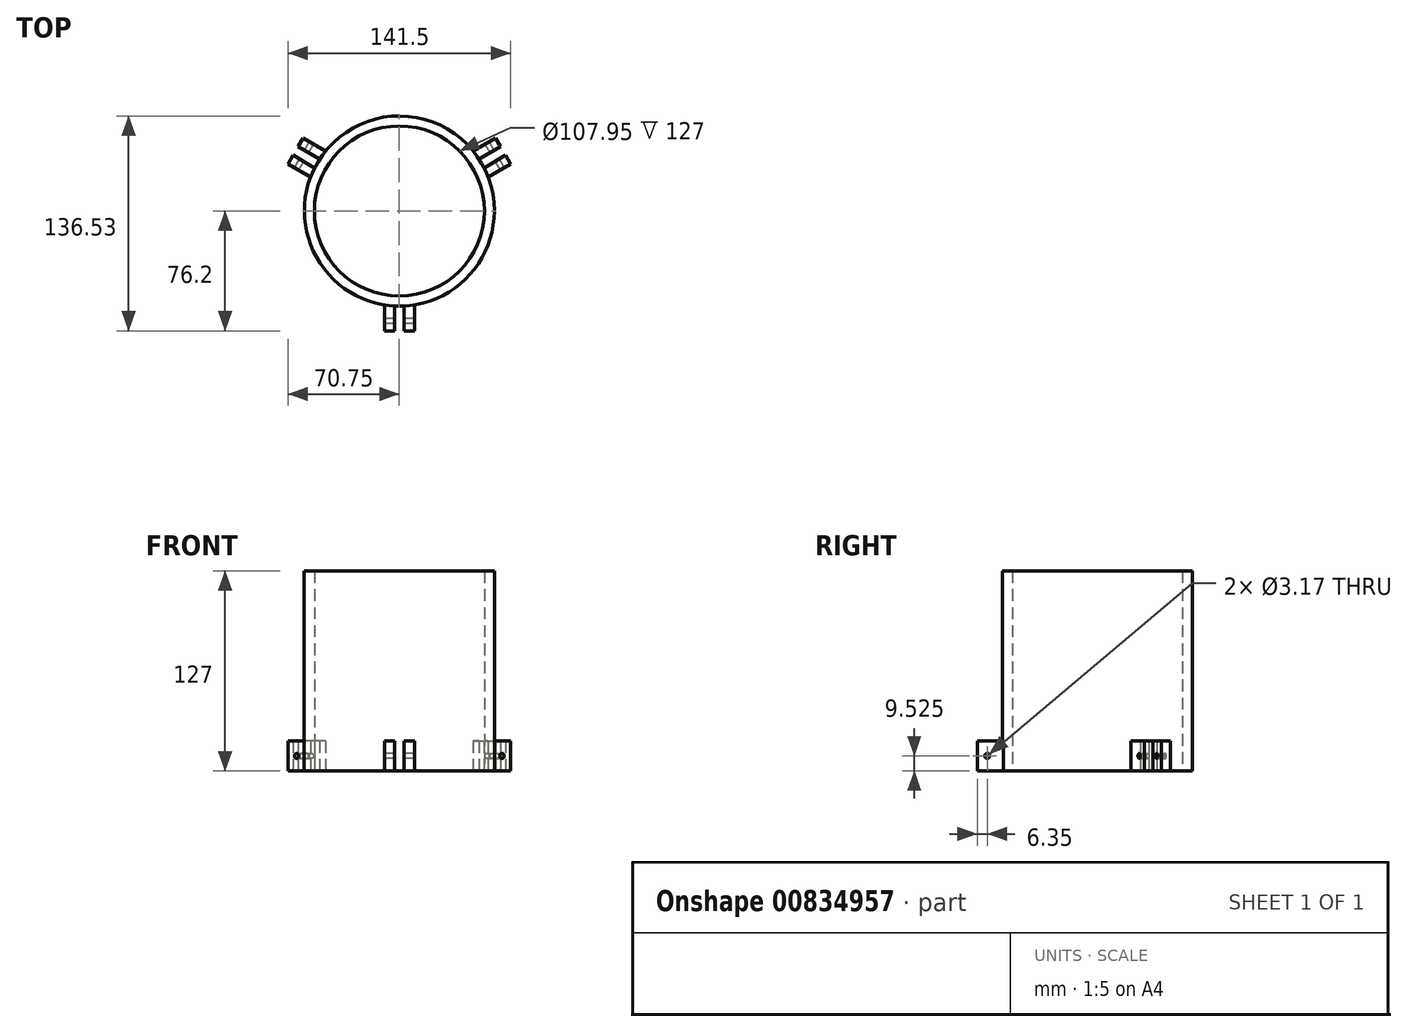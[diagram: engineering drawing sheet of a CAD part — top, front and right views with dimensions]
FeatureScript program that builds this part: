
annotation { "Feature Type Name" : "Feature", "Feature Type Description" : "" }
export const myFeature = defineFeature(function(context is Context, id is Id, definition is map)
    precondition{}
    {
        {
            var Q0;
            Q0=qCreatedBy(makeId("Top.planeOp"),FACE);
            var sketch = newSketch(context, id + "F0", { "sketchPlane" : qUnion([Q0])});
            skCircle(sketch, "E0", {"center": v(0, 0) * mm, "radius": 53.98 * mm});
            skSolve(sketch);
        }
        {
            var Q0;
            Q0=qCreatedBy(makeId("Top.planeOp"),FACE);
            var sketch = newSketch(context, id + "F1", { "sketchPlane" : qUnion([Q0])});
            skCircle(sketch, "E1", {"center": v(0, 0) * mm, "radius": 60.33 * mm});
            skSolve(sketch);
        }
        {
            var Q0;
            Q0=makeQuery(id+"F1.imprint","IMPRINT",FACE,{"disambiguationData":[TD([[makeQuery(id+"F1.imprint","IMPRINT",EDGE,{"derivedFrom":sQuery(id+"F1.wireOp",EDGE,"E1")}),1.0]])]});
            extrude(context, id + "F2", {"entities" : qUnion([Q0]), "depth" : 127 * mm, "offsetDistance" : 25.4 * mm});
        }
        {
            var Q0;
            Q0=makeQuery(id+"F0.imprint","IMPRINT",FACE,{"disambiguationData":[TD([[makeQuery(id+"F0.imprint","IMPRINT",EDGE,{"derivedFrom":sQuery(id+"F0.wireOp",EDGE,"E0")}),1.0]])]});
            extrude(context, id + "F3", {"entities" : qUnion([Q0]), "operationType" : NewBodyOperationType.REMOVE, "depth" : 184.9 * mm, "offsetDistance" : 25.4 * mm});
        }
        {
            var Q0;
            Q0=qCreatedBy(makeId("Top.planeOp"),FACE);
            var sketch = newSketch(context, id + "F4", { "sketchPlane" : qUnion([Q0])});
            skLineSegment(sketch, "E2", {"start": v(0, 0) * mm, "end": v(0, 76.2) * mm});
            skLineSegment(sketch, "E3", {"start": v(0, 0) * mm, "end": v(-66, 38.1) * mm});
            skLineSegment(sketch, "E4", {"start": v(0, 0) * mm, "end": v(66, 38.1) * mm});
            skLineSegment(sketch, "E5", {"start": v(0, 0) * mm, "end": v(0, -76.2) * mm});
            skPoint(sketch, "E6", {"position": v(-33, 19.05) * mm});
            skPoint(sketch, "E7", {"position": v(33, 19.05) * mm});
            skPoint(sketch, "E8", {"position": v(0, -38.1) * mm});
            skLineSegment(sketch, "E9.0", {"start": v(4.76, 8.25) * mm, "end": v(-61.23, 46.35) * mm});
            skLineSegment(sketch, "E10.0", {"start": v(-4.76, -8.25) * mm, "end": v(-70.75, 29.85) * mm});
            skLineSegment(sketch, "E11.0", {"start": v(4.76, -8.25) * mm, "end": v(70.75, 29.85) * mm});
            skLineSegment(sketch, "E12.0", {"start": v(-4.76, 8.25) * mm, "end": v(61.23, 46.35) * mm});
            skLineSegment(sketch, "E13.0", {"start": v(1.59, -2.75) * mm, "end": v(67.58, 35.35) * mm});
            skLineSegment(sketch, "E14.0", {"start": v(-1.59, 2.75) * mm, "end": v(64.4, 40.85) * mm});
            skLineSegment(sketch, "E15.0", {"start": v(1.59, 2.75) * mm, "end": v(-64.4, 40.85) * mm});
            skLineSegment(sketch, "E16.0", {"start": v(-1.59, -2.75) * mm, "end": v(-67.58, 35.35) * mm});
            skLineSegment(sketch, "E17.0", {"start": v(-9.53, 0) * mm, "end": v(-9.52, -76.2) * mm});
            skLineSegment(sketch, "E18.0", {"start": v(9.52, 0) * mm, "end": v(9.53, -76.2) * mm});
            skLineSegment(sketch, "E19.0", {"start": v(-3.18, 0) * mm, "end": v(-3.17, -76.2) * mm});
            skLineSegment(sketch, "E20.0", {"start": v(3.17, 0) * mm, "end": v(3.18, -76.2) * mm});
            skLineSegment(sketch, "E21", {"start": v(-70.75, 29.85) * mm, "end": v(-67.58, 35.35) * mm});
            skLineSegment(sketch, "E22", {"start": v(-64.4, 40.85) * mm, "end": v(-61.23, 46.35) * mm});
            skLineSegment(sketch, "E23", {"start": v(61.23, 46.35) * mm, "end": v(64.4, 40.85) * mm});
            skLineSegment(sketch, "E24", {"start": v(67.58, 35.35) * mm, "end": v(70.75, 29.85) * mm});
            skLineSegment(sketch, "E25", {"start": v(-9.52, -76.2) * mm, "end": v(-3.17, -76.2) * mm});
            skLineSegment(sketch, "E26", {"start": v(3.18, -76.2) * mm, "end": v(9.53, -76.2) * mm});
            skCircle(sketch, "E27", {"center": v(0, 0) * mm, "radius": 60.28 * mm});
            skSolve(sketch);
        }
        {
            var Q0;
            {var subQ0=sQuery(id+"F4.wireOp",EDGE,"E21");Q0=makeQuery(id+"F4.imprint","IMPRINT",FACE,{"disambiguationData":[TD([[makeQuery(id+"F4.imprint","IMPRINT",EDGE,{"derivedFrom":subQ0}),-1.0]])]});}
            var Q1;
            {var subQ0=sQuery(id+"F4.wireOp",EDGE,"E22");Q1=makeQuery(id+"F4.imprint","IMPRINT",FACE,{"disambiguationData":[TD([[makeQuery(id+"F4.imprint","IMPRINT",EDGE,{"derivedFrom":subQ0}),-1.0]])]});}
            var Q2;
            {var subQ0=sQuery(id+"F4.wireOp",EDGE,"E24");Q2=makeQuery(id+"F4.imprint","IMPRINT",FACE,{"disambiguationData":[TD([[makeQuery(id+"F4.imprint","IMPRINT",EDGE,{"derivedFrom":subQ0}),-1.0]])]});}
            var Q3;
            {var subQ0=sQuery(id+"F4.wireOp",EDGE,"E23");Q3=makeQuery(id+"F4.imprint","IMPRINT",FACE,{"disambiguationData":[TD([[makeQuery(id+"F4.imprint","IMPRINT",EDGE,{"derivedFrom":subQ0}),-1.0]])]});}
            var Q4;
            {var subQ0=sQuery(id+"F4.wireOp",EDGE,"E25");Q4=makeQuery(id+"F4.imprint","IMPRINT",FACE,{"disambiguationData":[TD([[makeQuery(id+"F4.imprint","IMPRINT",EDGE,{"derivedFrom":subQ0}),1.0]])]});}
            var Q5;
            {var subQ0=sQuery(id+"F4.wireOp",EDGE,"E26");Q5=makeQuery(id+"F4.imprint","IMPRINT",FACE,{"disambiguationData":[TD([[makeQuery(id+"F4.imprint","IMPRINT",EDGE,{"derivedFrom":subQ0}),1.0]])]});}
            extrude(context, id + "F5", {"entities" : qUnion([Q0, Q1, Q2, Q3, Q4, Q5]), "operationType" : NewBodyOperationType.ADD, "depth" : 19.05 * mm, "offsetDistance" : 25.4 * mm});
        }
        {
            var Q0;
            Q0=makeQuery(id+"F5.opExtrude","SWEPT_FACE",FACE,{"disambiguationData":[OSD([sQuery(id+"F4.wireOp",EDGE,"E9.0")])]});
            var sketch = newSketch(context, id + "F6", { "sketchPlane" : qUnion([Q0])});
            skCircle(sketch, "E28", {"center": v(69.85, 9.53) * mm, "radius": 1.59 * mm});
            skSolve(sketch);
        }
        {
            var Q0;
            Q0=makeQuery(id+"F6.imprint","IMPRINT",FACE,{"disambiguationData":[TD([[makeQuery(id+"F6.imprint","IMPRINT",EDGE,{"derivedFrom":sQuery(id+"F6.wireOp",EDGE,"E28")}),1.0]])]});
            extrude(context, id + "F7", {"entities" : qUnion([Q0]), "operationType" : NewBodyOperationType.REMOVE, "oppositeDirection" : true, "depth" : 25.4 * mm, "offsetDistance" : 25.4 * mm});
        }
        {
            var Q0;
            Q0=makeQuery(id+"F5.opExtrude","SWEPT_FACE",FACE,{"disambiguationData":[OSD([sQuery(id+"F4.wireOp",EDGE,"E11.0")])]});
            var sketch = newSketch(context, id + "F8", { "sketchPlane" : qUnion([Q0])});
            skLineSegment(sketch, "E29.bottom", {"start": v(76.2, 0) * mm, "end": v(59.57, 0) * mm});
            skLineSegment(sketch, "E29.top", {"start": v(76.2, 19.05) * mm, "end": v(59.57, 19.05) * mm});
            skLineSegment(sketch, "E29.left", {"start": v(76.2, 0) * mm, "end": v(76.2, 19.05) * mm});
            skLineSegment(sketch, "E29.right", {"start": v(59.57, 0) * mm, "end": v(59.57, 19.05) * mm});
            skCircle(sketch, "E30", {"center": v(69.85, 9.53) * mm, "radius": 1.59 * mm});
            skSolve(sketch);
        }
        {
            var Q0;
            Q0=makeQuery(id+"F8.imprint","IMPRINT",FACE,{"disambiguationData":[TD([[makeQuery(id+"F8.imprint","IMPRINT",EDGE,{"derivedFrom":sQuery(id+"F8.wireOp",EDGE,"E30")}),1.0]])]});
            extrude(context, id + "F9", {"entities" : qUnion([Q0]), "operationType" : NewBodyOperationType.REMOVE, "oppositeDirection" : true, "depth" : 25.4 * mm, "offsetDistance" : 25.4 * mm});
        }
        {
            var Q0;
            Q0=makeQuery(id+"F5.opExtrude","SWEPT_FACE",FACE,{"disambiguationData":[OSD([sQuery(id+"F4.wireOp",EDGE,"E17.0")])]});
            var sketch = newSketch(context, id + "F10", { "sketchPlane" : qUnion([Q0])});
            skLineSegment(sketch, "E31.bottom", {"start": v(76.2, 0) * mm, "end": v(59.57, 0) * mm});
            skLineSegment(sketch, "E31.top", {"start": v(76.2, 19.05) * mm, "end": v(59.57, 19.05) * mm});
            skLineSegment(sketch, "E31.left", {"start": v(76.2, 0) * mm, "end": v(76.2, 19.05) * mm});
            skLineSegment(sketch, "E31.right", {"start": v(59.57, 0) * mm, "end": v(59.57, 19.05) * mm});
            skCircle(sketch, "E32", {"center": v(69.85, 9.53) * mm, "radius": 1.59 * mm});
            skSolve(sketch);
        }
        {
            var Q0;
            Q0=makeQuery(id+"F10.imprint","IMPRINT",FACE,{"disambiguationData":[TD([[makeQuery(id+"F10.imprint","IMPRINT",EDGE,{"derivedFrom":sQuery(id+"F10.wireOp",EDGE,"E32")}),1.0]])]});
            extrude(context, id + "F11", {"entities" : qUnion([Q0]), "operationType" : NewBodyOperationType.REMOVE, "oppositeDirection" : true, "depth" : 36.65 * mm, "offsetDistance" : 25.4 * mm});
        }
    });
